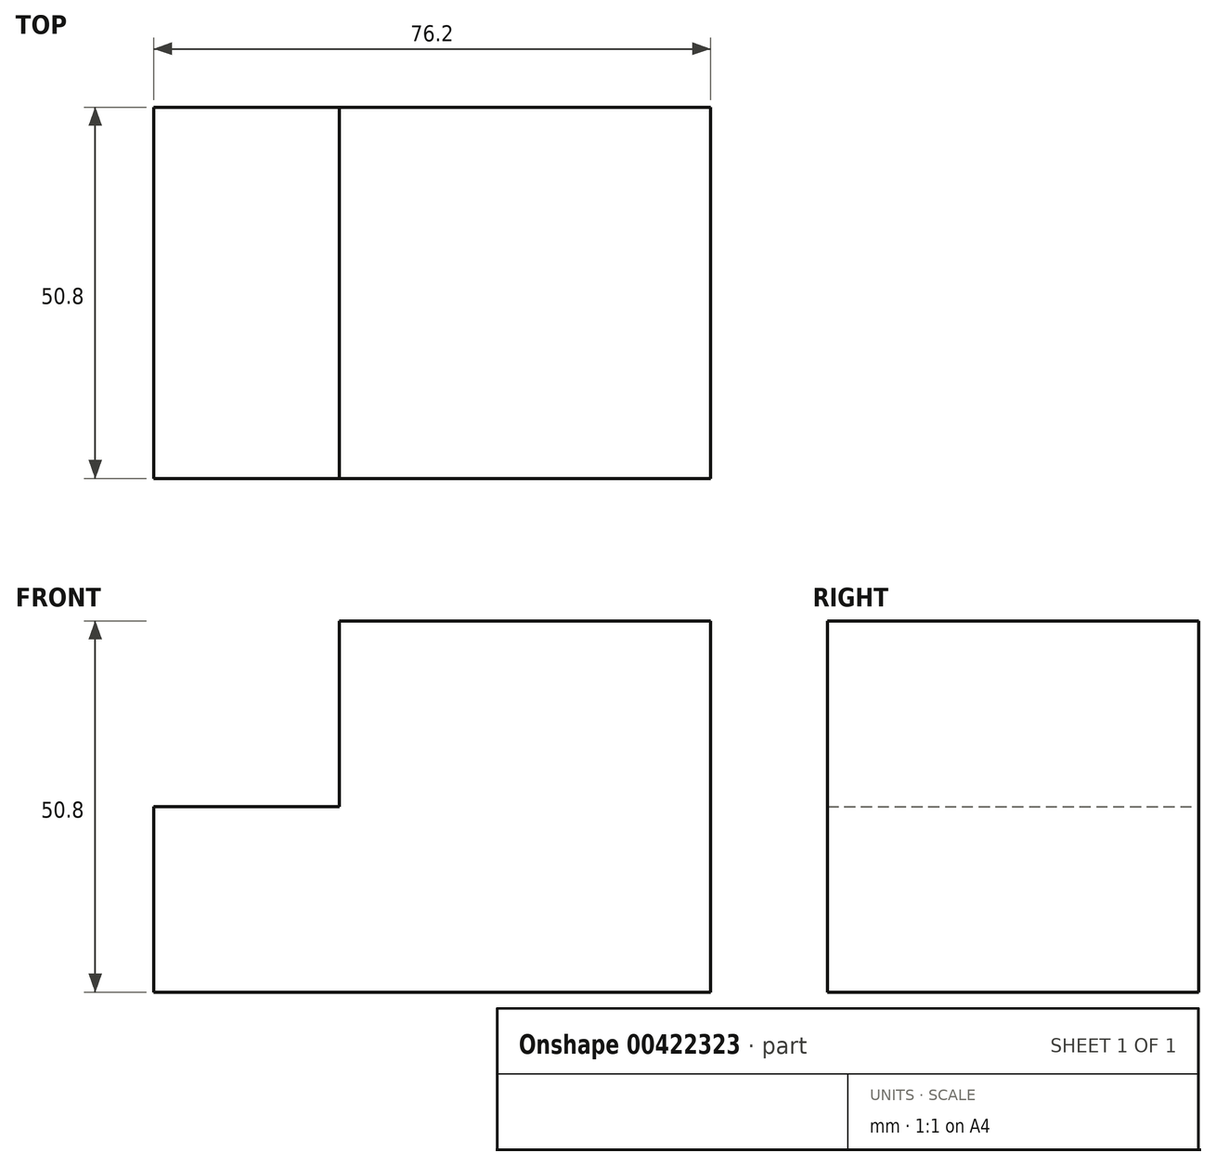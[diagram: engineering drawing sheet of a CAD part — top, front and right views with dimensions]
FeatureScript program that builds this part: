
annotation { "Feature Type Name" : "Feature", "Feature Type Description" : "" }
export const myFeature = defineFeature(function(context is Context, id is Id, definition is map)
    precondition{}
    {
        {
            var Q0;
            Q0=qCreatedBy(makeId("Front.planeOp"),FACE);
            var sketch = newSketch(context, id + "F0", { "sketchPlane" : qUnion([Q0])});
            skLineSegment(sketch, "E0.bottom", {"start": v(10.93, -11.15) * mm, "end": v(61.73, -11.15) * mm});
            skLineSegment(sketch, "E0.top", {"start": v(10.93, -61.95) * mm, "end": v(61.73, -61.95) * mm});
            skLineSegment(sketch, "E0.left", {"start": v(10.93, -11.15) * mm, "end": v(10.93, -61.95) * mm});
            skLineSegment(sketch, "E0.right", {"start": v(61.73, -11.15) * mm, "end": v(61.73, -61.95) * mm});
            skLineSegment(sketch, "E1.bottom", {"start": v(-14.47, -36.55) * mm, "end": v(10.93, -36.55) * mm});
            skLineSegment(sketch, "E1.top", {"start": v(-14.47, -61.95) * mm, "end": v(10.93, -61.95) * mm});
            skLineSegment(sketch, "E1.left", {"start": v(-14.47, -36.55) * mm, "end": v(-14.47, -61.95) * mm});
            skLineSegment(sketch, "E1.right", {"start": v(10.93, -36.55) * mm, "end": v(10.93, -61.95) * mm});
            skSolve(sketch);
        }
        {
            var Q0;
            Q0=makeQuery(id+"F0.imprint","IMPRINT",FACE,{"disambiguationData":[TD([[makeQuery(id+"F0.imprint","IMPRINT",EDGE,{"derivedFrom":sQuery(id+"F0.wireOp",EDGE,"E0.bottom")}),-1.0]])]});
            var Q1;
            Q1=makeQuery(id+"F0.imprint","IMPRINT",FACE,{"disambiguationData":[TD([[makeQuery(id+"F0.imprint","IMPRINT",EDGE,{"derivedFrom":sQuery(id+"F0.wireOp",EDGE,"E1.bottom")}),-1.0]])]});
            extrude(context, id + "F1", {"entities" : qUnion([Q0, Q1]), "depth" : 50.8 * mm});
        }
    });
